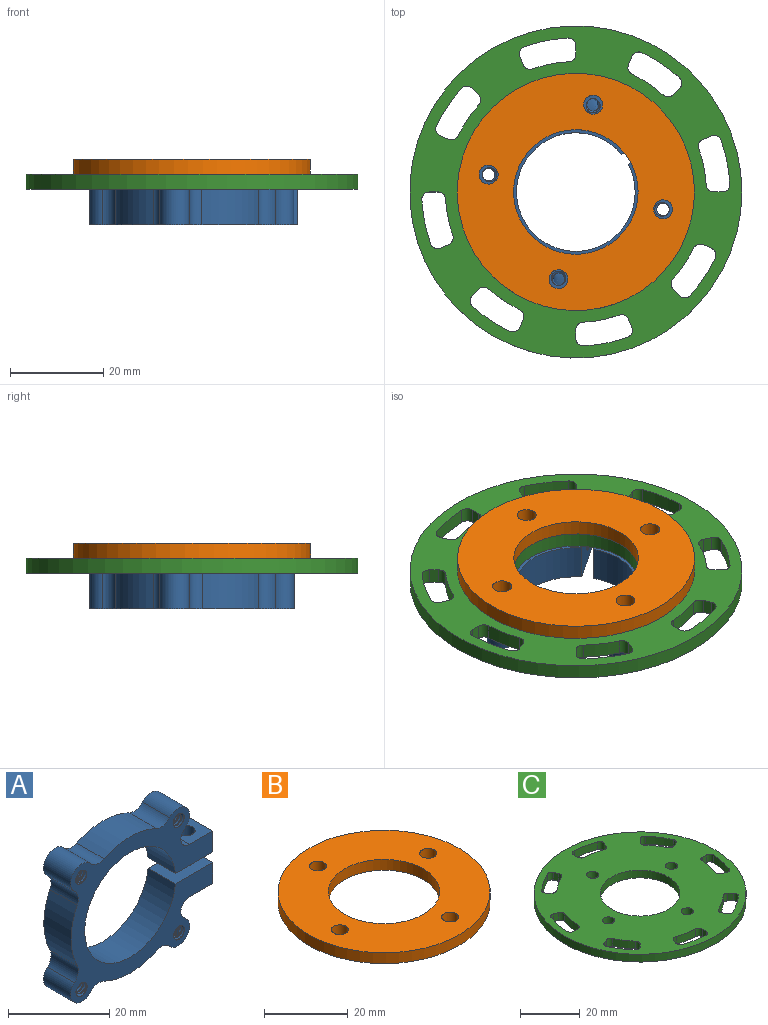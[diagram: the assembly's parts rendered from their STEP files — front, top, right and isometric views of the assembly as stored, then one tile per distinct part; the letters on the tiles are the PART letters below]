
ASSEMBLY  parts=3 mates=6
PART A: 47 faces, bbox 39.9x8.5x33.5 mm
  f0: cylinder r=1.75mm len=7.62mm, axis (0,-1,0), area 10.5mm2, adj f17,f18,f45,f46
  f1: cylinder r=1.75mm len=5.08mm, axis (0,0,1), area 7mm2, adj f19,f20,f43,f44
  f2: cylinder r=1.75mm len=7.62mm, axis (0,-1,0), area 10.5mm2, adj f17,f18,f41,f42
  f3: cylinder r=1.75mm len=7.62mm, axis (0,-1,0), area 10.5mm2, adj f17,f18,f39,f40
  f4: cylinder r=1.75mm len=7.62mm, axis (0,-1,0), area 10.5mm2, adj f17,f18,f37,f38
  f5: cylinder r=1.35mm len=5.08mm, axis (0,0,1), area 12.6mm2, adj f19,f20,f43,f44
  f6: cylinder r=1.78mm len=5.08mm, axis (0,0,1), area 56.8mm2, adj f25,f26
  f7: cylinder r=3.17mm len=7.62mm, axis (0,1,0), area 31.6mm2, adj f15,f16,f17,f18
  f8: cylinder r=3.17mm len=7.62mm, axis (0,1,0), area 31.6mm2, adj f14,f15,f17,f18
  f9: cylinder r=1.35mm len=7.62mm, axis (0,1,0), area 19mm2, adj f17,f18,f45,f46
  f10: cylinder r=1.35mm len=7.62mm, axis (0,1,0), area 19mm2, adj f17,f18,f37,f38
  f11: cylinder r=1.35mm len=7.62mm, axis (0,1,0), area 19mm2, adj f17,f18,f39,f40
  f12: cylinder r=1.35mm len=7.62mm, axis (0,1,0), area 19mm2, adj f17,f18,f41,f42
  f13: cylinder r=12.7mm len=25.4mm, axis (0,-1,0), area 588.7mm2, adj f17,f18,f19,f25
  f14: cylinder r=3.17mm len=7.62mm, axis (0,-1,0), area 79.2mm2, adj f8,f17,f18,f30
  f15: cylinder r=16.51mm len=14.59mm, axis (0,-1,0), area 115.2mm2, adj f7,f8,f17,f18
  f16: cylinder r=3.17mm len=7.62mm, axis (0,-1,0), area 79.2mm2, adj f7,f17,f18,f35
  f17: plane 39.89x33.48mm, normal (0,1,0), area 519.9mm2, adj f0,f2,f3,f4,f7,f8,f9,f10
  f18: plane 39.89x33.48mm, normal (0,-1,0), area 519.9mm2, adj f0,f2,f3,f4,f7,f8,f9,f10
  f19: plane 10.61x7.81mm, normal (0,0,1), area 72.1mm2, adj f1,f5,f13,f17,f18,f28,f43,f44
  f20: plane 7.81x6.64mm, normal (0,0,-1), area 41.8mm2, adj f1,f5,f17,f18,f28,f36,f43,f44
  f21: cylinder r=16.51mm len=14.59mm, axis (0,-1,0), area 115.2mm2, adj f17,f18,f31,f32
  f22: cylinder r=3.17mm len=7.62mm, axis (0,-1,0), area 79.2mm2, adj f17,f18,f31,f34
  f23: cylinder r=16.51mm len=14.59mm, axis (0,-1,0), area 115.2mm2, adj f17,f18,f29,f30
  f24: cylinder r=3.17mm len=7.62mm, axis (0,-1,0), area 79.2mm2, adj f17,f18,f29,f32
  f25: plane 10.42x7.62mm, normal (0,0,-1), area 69.5mm2, adj f6,f13,f17,f18,f27
  f26: plane 7.62x6.45mm, normal (0,0,1), area 39.2mm2, adj f6,f17,f18,f27,f33
  f27: plane 7.62x5.08mm, normal (1,0,0), area 38.7mm2, adj f17,f18,f25,f26
  f28: plane 7.62x5.08mm, normal (1,0,0), area 38.7mm2, adj f17,f18,f19,f20
  f29: cylinder r=3.17mm len=7.62mm, axis (0,1,0), area 31.6mm2, adj f17,f18,f23,f24
  f30: cylinder r=3.17mm len=7.62mm, axis (0,1,0), area 31.6mm2, adj f14,f17,f18,f23
  f31: cylinder r=3.17mm len=7.62mm, axis (0,1,0), area 31.6mm2, adj f17,f18,f21,f22
  f32: cylinder r=3.17mm len=7.62mm, axis (0,1,0), area 31.6mm2, adj f17,f18,f21,f24
  f33: cylinder r=2.42mm len=7.62mm, axis (0,-1,0), area 44.7mm2, adj f17,f18,f26,f34
  f34: plane 7.62x0.56mm, normal (0.66,0,-0.75), area 5.6mm2, adj f17,f18,f22,f33
  f35: plane 7.62x0.56mm, normal (0.66,0,0.75), area 5.6mm2, adj f16,f17,f18,f36
  f36: cylinder r=2.42mm len=7.62mm, axis (0,-1,0), area 44.7mm2, adj f17,f18,f20,f35
  f37: bspline ~8.24x4.04mm, area 43.4mm2, adj f4,f10,f17,f18
  f38: bspline ~8.28x3.5mm, area 56.5mm2, adj f4,f10,f17,f18
  f39: bspline ~8.24x4.04mm, area 43.4mm2, adj f3,f11,f17,f18
  f40: bspline ~8.08x3.5mm, area 43.4mm2, adj f3,f11,f17,f18
  f41: bspline ~8.24x4.04mm, area 43.4mm2, adj f2,f12,f17,f18
  f42: bspline ~8.28x3.5mm, area 56.5mm2, adj f2,f12,f17,f18
  f43: bspline ~5.54x3.5mm, area 28.9mm2, adj f1,f5,f19,f20
  f44: bspline ~5.54x3.5mm, area 28.9mm2, adj f1,f5,f19,f20
  f45: bspline ~8.24x4.04mm, area 43.4mm2, adj f0,f9,f17,f18
  f46: bspline ~8.08x3.5mm, area 43.4mm2, adj f0,f9,f17,f18
PART B: 8 faces, bbox 50.8x50.8x3.2 mm
  f0: cylinder r=2.03mm len=4.06mm, axis (0,0,1), area 40.5mm2, adj f6,f7
  f1: cylinder r=2.03mm len=4.06mm, axis (0,0,1), area 40.5mm2, adj f6,f7
  f2: cylinder r=2.03mm len=4.06mm, axis (0,0,1), area 40.5mm2, adj f6,f7
  f3: cylinder r=2.03mm len=4.06mm, axis (0,0,1), area 40.5mm2, adj f6,f7
  f4: cylinder r=13.33mm len=26.67mm, axis (0,0,1), area 266mm2, adj f6,f7
  f5: cylinder r=25.4mm len=50.8mm, axis (0,0,1), area 506.7mm2, adj f6,f7
  f6: plane 50.8x50.8mm, normal (0,0,-1), area 1416.3mm2, adj f0,f1,f2,f3,f4,f5
  f7: plane 50.8x50.8mm, normal (0,0,1), area 1416.3mm2, adj f0,f1,f2,f3,f4,f5
PART C: 72 faces, bbox 71.1x71.1x3.2 mm
  f0: plane 3.18x1.76mm, normal (-0.38,0.92,0), area 6.1mm2, adj f38,f39,f68,f71
  f1: cylinder r=27.94mm len=6.6mm, axis (0,0,-1), area 25.3mm2, adj f38,f39,f68,f69
  f2: plane 3.18x1.35mm, normal (0.71,-0.71,0), area 6.1mm2, adj f38,f39,f69,f70
  f3: plane 3.18x1.76mm, normal (0.38,0.92,0), area 6.1mm2, adj f38,f39,f64,f67
  f4: cylinder r=27.94mm len=7.79mm, axis (0,0,-1), area 25.3mm2, adj f38,f39,f64,f65
  f5: plane 3.18x1.91mm, normal (0,-1,0), area 6.1mm2, adj f38,f39,f65,f66
  f6: plane 3.18x1.76mm, normal (0.92,0.38,0), area 6.1mm2, adj f38,f39,f60,f63
  f7: cylinder r=27.94mm len=6.6mm, axis (0,0,-1), area 25.3mm2, adj f38,f39,f60,f61
  f8: plane 3.18x1.35mm, normal (-0.71,-0.71,0), area 6.1mm2, adj f38,f39,f61,f62
  f9: plane 3.18x1.76mm, normal (0.92,-0.38,0), area 6.1mm2, adj f38,f39,f56,f59
  f10: cylinder r=27.94mm len=7.79mm, axis (0,0,-1), area 25.3mm2, adj f38,f39,f56,f57
  f11: plane 3.18x1.91mm, normal (-1,0,0), area 6.1mm2, adj f38,f39,f57,f58
  f12: plane 3.18x1.76mm, normal (0.38,-0.92,0), area 6.1mm2, adj f38,f39,f52,f55
  f13: cylinder r=27.94mm len=6.6mm, axis (0,0,-1), area 25.3mm2, adj f38,f39,f52,f53
  f14: plane 3.18x1.35mm, normal (-0.71,0.71,0), area 6.1mm2, adj f38,f39,f53,f54
  f15: plane 3.18x1.76mm, normal (-0.38,-0.92,0), area 6.1mm2, adj f38,f39,f48,f51
  f16: cylinder r=27.94mm len=7.79mm, axis (0,0,-1), area 25.3mm2, adj f38,f39,f48,f49
  f17: plane 3.18x1.91mm, normal (0,1,0), area 6.1mm2, adj f38,f39,f49,f50
  f18: plane 3.18x1.76mm, normal (-0.92,-0.38,0), area 6.1mm2, adj f38,f39,f44,f47
  f19: cylinder r=27.94mm len=6.6mm, axis (0,0,-1), area 25.3mm2, adj f38,f39,f44,f45
  f20: plane 3.18x1.35mm, normal (0.71,0.71,0), area 6.1mm2, adj f38,f39,f45,f46
  f21: plane 3.18x1.76mm, normal (-0.92,0.38,0), area 6.1mm2, adj f38,f39,f40,f43
  f22: cylinder r=27.94mm len=7.79mm, axis (0,0,-1), area 25.3mm2, adj f38,f39,f40,f41
  f23: plane 3.18x1.91mm, normal (1,0,0), area 6.1mm2, adj f38,f39,f41,f42
  f24: cylinder r=2.03mm len=4.06mm, axis (0,0,-1), area 40.5mm2, adj f38,f39
  f25: cylinder r=2.03mm len=4.06mm, axis (0,0,-1), area 40.5mm2, adj f38,f39
  f26: cylinder r=2.03mm len=4.06mm, axis (0,0,-1), area 40.5mm2, adj f38,f39
  f27: cylinder r=13.33mm len=26.67mm, axis (0,0,-1), area 266mm2, adj f38,f39
  f28: cylinder r=35.56mm len=71.12mm, axis (0,0,-1), area 709.4mm2, adj f38,f39
  f29: cylinder r=33.02mm len=7.98mm, axis (0,0,-1), area 30.6mm2, adj f38,f39,f70,f71
  f30: cylinder r=33.02mm len=9.41mm, axis (0,0,-1), area 30.6mm2, adj f38,f39,f66,f67
  f31: cylinder r=33.02mm len=7.98mm, axis (0,0,-1), area 30.6mm2, adj f38,f39,f62,f63
  f32: cylinder r=33.02mm len=9.41mm, axis (0,0,-1), area 30.6mm2, adj f38,f39,f58,f59
  f33: cylinder r=33.02mm len=7.98mm, axis (0,0,-1), area 30.6mm2, adj f38,f39,f54,f55
  f34: cylinder r=33.02mm len=9.41mm, axis (0,0,-1), area 30.6mm2, adj f38,f39,f50,f51
  f35: cylinder r=33.02mm len=7.98mm, axis (0,0,-1), area 30.6mm2, adj f38,f39,f46,f47
  f36: cylinder r=33.02mm len=9.41mm, axis (0,0,-1), area 30.6mm2, adj f38,f39,f42,f43
  f37: cylinder r=2.03mm len=4.06mm, axis (0,0,-1), area 40.5mm2, adj f38,f39
  f38: plane 71.12x71.12mm, normal (0,0,1), area 2892.9mm2, adj f0,f1,f2,f3,f4,f5,f6,f7
  f39: plane 71.12x71.12mm, normal (0,0,-1), area 2892.9mm2, adj f0,f1,f2,f3,f4,f5,f6,f7
  f40: cylinder r=1.59mm len=3.18mm, axis (0,0,-1), area 7.6mm2, adj f21,f22,f38,f39
  f41: cylinder r=1.59mm len=3.18mm, axis (0,0,-1), area 7.6mm2, adj f22,f23,f38,f39
  f42: cylinder r=1.59mm len=3.18mm, axis (0,0,-1), area 8.2mm2, adj f23,f36,f38,f39
  f43: cylinder r=1.59mm len=3.18mm, axis (0,0,-1), area 8.2mm2, adj f21,f36,f38,f39
  f44: cylinder r=1.59mm len=3.18mm, axis (0,0,-1), area 7.6mm2, adj f18,f19,f38,f39
  f45: cylinder r=1.59mm len=3.18mm, axis (0,0,-1), area 7.6mm2, adj f19,f20,f38,f39
  f46: cylinder r=1.59mm len=3.18mm, axis (0,0,-1), area 8.2mm2, adj f20,f35,f38,f39
  f47: cylinder r=1.59mm len=3.18mm, axis (0,0,-1), area 8.2mm2, adj f18,f35,f38,f39
  f48: cylinder r=1.59mm len=3.18mm, axis (0,0,-1), area 7.6mm2, adj f15,f16,f38,f39
  f49: cylinder r=1.59mm len=3.18mm, axis (0,0,-1), area 7.6mm2, adj f16,f17,f38,f39
  f50: cylinder r=1.59mm len=3.18mm, axis (0,0,-1), area 8.2mm2, adj f17,f34,f38,f39
  f51: cylinder r=1.59mm len=3.18mm, axis (0,0,-1), area 8.2mm2, adj f15,f34,f38,f39
  f52: cylinder r=1.59mm len=3.18mm, axis (0,0,-1), area 7.6mm2, adj f12,f13,f38,f39
  f53: cylinder r=1.59mm len=3.18mm, axis (0,0,-1), area 7.6mm2, adj f13,f14,f38,f39
  f54: cylinder r=1.59mm len=3.18mm, axis (0,0,-1), area 8.2mm2, adj f14,f33,f38,f39
  f55: cylinder r=1.59mm len=3.18mm, axis (0,0,-1), area 8.2mm2, adj f12,f33,f38,f39
  f56: cylinder r=1.59mm len=3.18mm, axis (0,0,-1), area 7.6mm2, adj f9,f10,f38,f39
  f57: cylinder r=1.59mm len=3.18mm, axis (0,0,-1), area 7.6mm2, adj f10,f11,f38,f39
  f58: cylinder r=1.59mm len=3.18mm, axis (0,0,-1), area 8.2mm2, adj f11,f32,f38,f39
  f59: cylinder r=1.59mm len=3.18mm, axis (0,0,-1), area 8.2mm2, adj f9,f32,f38,f39
  f60: cylinder r=1.59mm len=3.18mm, axis (0,0,-1), area 7.6mm2, adj f6,f7,f38,f39
  f61: cylinder r=1.59mm len=3.18mm, axis (0,0,-1), area 7.6mm2, adj f7,f8,f38,f39
  f62: cylinder r=1.59mm len=3.18mm, axis (0,0,-1), area 8.2mm2, adj f8,f31,f38,f39
  f63: cylinder r=1.59mm len=3.18mm, axis (0,0,-1), area 8.2mm2, adj f6,f31,f38,f39
  f64: cylinder r=1.59mm len=3.18mm, axis (0,0,-1), area 7.6mm2, adj f3,f4,f38,f39
  f65: cylinder r=1.59mm len=3.18mm, axis (0,0,-1), area 7.6mm2, adj f4,f5,f38,f39
  f66: cylinder r=1.59mm len=3.18mm, axis (0,0,-1), area 8.2mm2, adj f5,f30,f38,f39
  f67: cylinder r=1.59mm len=3.18mm, axis (0,0,-1), area 8.2mm2, adj f3,f30,f38,f39
  f68: cylinder r=1.59mm len=3.18mm, axis (0,0,-1), area 7.6mm2, adj f0,f1,f38,f39
  f69: cylinder r=1.59mm len=3.18mm, axis (0,0,-1), area 7.6mm2, adj f1,f2,f38,f39
  f70: cylinder r=1.59mm len=3.18mm, axis (0,0,-1), area 8.2mm2, adj f2,f29,f38,f39
  f71: cylinder r=1.59mm len=3.18mm, axis (0,0,-1), area 8.2mm2, adj f0,f29,f38,f39
PLACE A rot(axis=(0.92,0.28,0.28),94.8deg) t=(64.82,27.97,-39.64)mm
PLACE B rot(axis=(-1,0,0),180deg) t=(64.82,27.97,-28.84)mm
PLACE C rot(axis=(-1,0,0),180deg) t=(64.82,27.97,-28.84)mm fixed
MATE cylindrical A.f13 <-> C.f1  axis (0,0,-1) through (64.82,27.97,-35.83)mm
MATE cylindrical C.f26 <-> B.f3  axis (0,0,1) through (61.11,9.28,-30.43)mm
MATE planar B.f4 <-> C.f1  axis (0,0,-1) through (64.82,27.97,-28.84)mm
MATE planar C.f1 <-> A.f17  axis (0,0,-1) through (64.82,27.97,-32.02)mm
MATE cylindrical A.f3 <-> B.f1  axis (0,0,-1) through (46.14,31.69,-35.83)mm
MATE cylindrical B.f4 <-> C.f1  axis (0,0,-1) through (64.82,27.97,-27.26)mm
